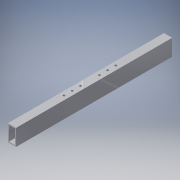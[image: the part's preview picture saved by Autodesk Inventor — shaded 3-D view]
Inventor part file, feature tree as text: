
AUTODESK INVENTOR PART (.ipt)
format: ipt  version: 2016 (Build 200138000, 138)  size: 110,080 bytes
history: native  units: in
note: dims shown in document units (in); Inventor stores cm internally (conversion verified against a paired STEP export)
features: extrude x1, sketch x1
ambient origin geometry x8: Origin, YZ Plane, XZ Plane, XY Plane, X Axis, Y Axis, Z Axis, Center Point
bodies: Solid1 (feature_tree)
feature tree (2):
  extrude  "Extrusion1"  Depth=2.0in
  sketch  "Sketch1"  dims[d0=1.0in d1=2.0in d2=0.125in d3=19.0in d4=0.0in]
